# Revit family: BOS_Duplex-Zarge-DIN-L_Familie
name_source: partatom
category: Türen
revit_build: Autodesk Revit 2017 (Build: 20160225_1515(x64)
units: mm (PartAtom-declared; Revit-internal decimal feet)

## family parameters
Basisbauteil = Wand
Beim Laden mit Abzugskörper schneiden = Nein
Gemeinsam genutzt = Nein
Immer vertikal = Ja
Raumberechnungspunkt = Ja

## types (2) — shared parameters
Acrylfuge = 5 mm  [stored 0.0164042 ft]
BBL1 Bandbezugslinie   Hinge Position 1 = 241 mm  [stored 0.790682 ft]
BE max. = 100 mm  [stored 0.328084 ft]
Bauelement = BOS Stahlzarge
Beschreibung = 2-schalige Duplex-Zarge als Blockprofil für Mauerwerk DIN links
Blechstärke = 1.5 mm  [stored 0.00492126 ft]
Dichtung 1 = Ja
Dichtung 2 = Ja
Doppelfalz = Nein
Drehpunkt Warnung sichtbar = Ja
Drehpunktabstand (SpM) horizontal = 15.75 mm  [stored 0.0516732 ft]
Drehpunktabstand (SpM) vertikal = 13.75 mm  [stored 0.0451115 ft]
Drehpunktreferenz horizontal = 500 mm  [stored 1.64042 ft]
Einfachfalz = Ja
Einfügepunkt 2 links = 17 mm  [stored 0.0557743 ft]
FMB max. = 1342 mm  [stored 4.40289 ft]
FMB min. = 591 mm  [stored 1.93898 ft]
FMH max. = 2858 mm  [stored 9.37664 ft]
FMH min. = 1608 mm  [stored 5.27559 ft]
Falzaufschlag = 15 mm  [stored 0.0492126 ft]
Falzaufschlag gesamt = 15 mm  [stored 0.0492126 ft]
Falztiefe 1 = 52 mm  [stored 0.170604 ft]
Falztiefe 2 = 52.5 mm  [stored 0.172244 ft]
Funktion = Innen
GT max. = 344 mm  [stored 1.12861 ft]
Gefälzt = Nein
Hersteller = BOS GmbH Best Of Steel, Lütkenfelde 4, D-48282 Emsdetten
Info-Texte sichtbar = Ja
Information in English = Nein
MW1 min. = 100 mm  [stored 0.328084 ft]
Material = grundiert, feuerverzinktes Feinblech nach DIN EN 10143
Material - Acrylfuge = <Nach Kategorie>
Material - Bänder = <Nach Kategorie>
Material - Dichtung = <Nach Kategorie>
Material - Drückergarnitur = <Nach Kategorie>
Material - Schließblech = <Nach Kategorie>
Material - Türblatt = <Nach Kategorie>
Material - Zarge = <Nach Kategorie>
Modell = Duplex
Putzwinkel max. = 28 mm  [stored 0.0918635 ft]
Putzwinkel min. = 10 mm  [stored 0.0328084 ft]
Sickentiefe = 11 mm  [stored 0.0360892 ft]
Spiegel Mittelteil horizontal = 30 mm  [stored 0.0984252 ft]
Spiegel Mittelteil vertikal = 25 mm  [stored 0.082021 ft]
Spiegel hinten max. = 60 mm  [stored 0.19685 ft]
Spiegel hinten min. = 60 mm  [stored 0.19685 ft]
Spiegel hinten mittel max. = 22 mm  [stored 0.0721785 ft]
Spiegel hinten mittel min. = 22 mm  [stored 0.0721785 ft]
Spiegel vorne max. = 45 mm  [stored 0.147638 ft]
Spiegel vorne min. = 45 mm  [stored 0.147638 ft]
Stumpf = Ja
Technische Infos rund um die Stahlzarge = www.BestOfSteel.de/tools-downloads/technische-infos-rund-um-die-stahlzarge/
Typenbild = <Keine Auswahl>
Türblattabstand 1 = -7.5 mm  [stored -0.0246063 ft]
Türblattabstand 2 = 4.5 mm  [stored 0.0147638 ft]
Türblattabstand 3 = 4.5 mm  [stored 0.0147638 ft]
Türblattabstand links-rechts = 3.5 mm  [stored 0.0114829 ft]
Türblattabstand oben = 4 mm  [stored 0.0131234 ft]
Türblattabstand unten = 7 mm  [stored 0.0229659 ft]
Türblattaufschlag = 13 mm
Türblattstärke = 40 mm  [stored 0.131234 ft]
Türblattstärke 2 = 40 mm  [stored 0.131234 ft]
Türblattversatz  horizontal = 16.25 mm  [stored 0.0533136 ft]
Türblattversatz vertikal = -18.75 mm
URL = www.BestOfSteel.de/stahlzargen/zargen-fuer-drehfluegeltueren/duplex-zargen
Öffnungswinkel max. = 90.00°
Öffnungswinkel min. = 0.00°
zero-valued in all types: Breite, Dicke, Falztiefe gesamt, Rohbaubreite, Rohbauhöhe, Türblattstärke 1, Türblattstärke 3

## per-type parameters (varying)
| type | Duplex für Mauerwerk | Duplex für Ständerwerk | Einfügepunkt 1 rechts | Einfügepunkt 2 rechts | Mauerwerk | Ständerwerk | Unterfütterung Wand 1 rechts | Unterfütterungsstärke 1 rechts | Unterfütterungsstärke 2 rechts |
| Duplex für Ständerwerk DIN links | Nein | Ja | 32 mm  [stored 0.104987 ft] | 17 mm  [stored 0.0557743 ft] | Nein | Ja | Ja | 15 mm  [stored 0.0492126 ft] | 13.5 mm |
| Duplex für Mauerwerk DIN links | Ja | Nein | 17 mm  [stored 0.0557743 ft] | 31 mm  [stored 0.101706 ft] | Ja | Nein | Nein | 0 mm  [stored 0 ft] | 27.5 mm  [stored 0.0902231 ft] |

note: [stored X ft] marks values corroborated as IEEE doubles in the binary element streams (Revit-internal decimal feet)
